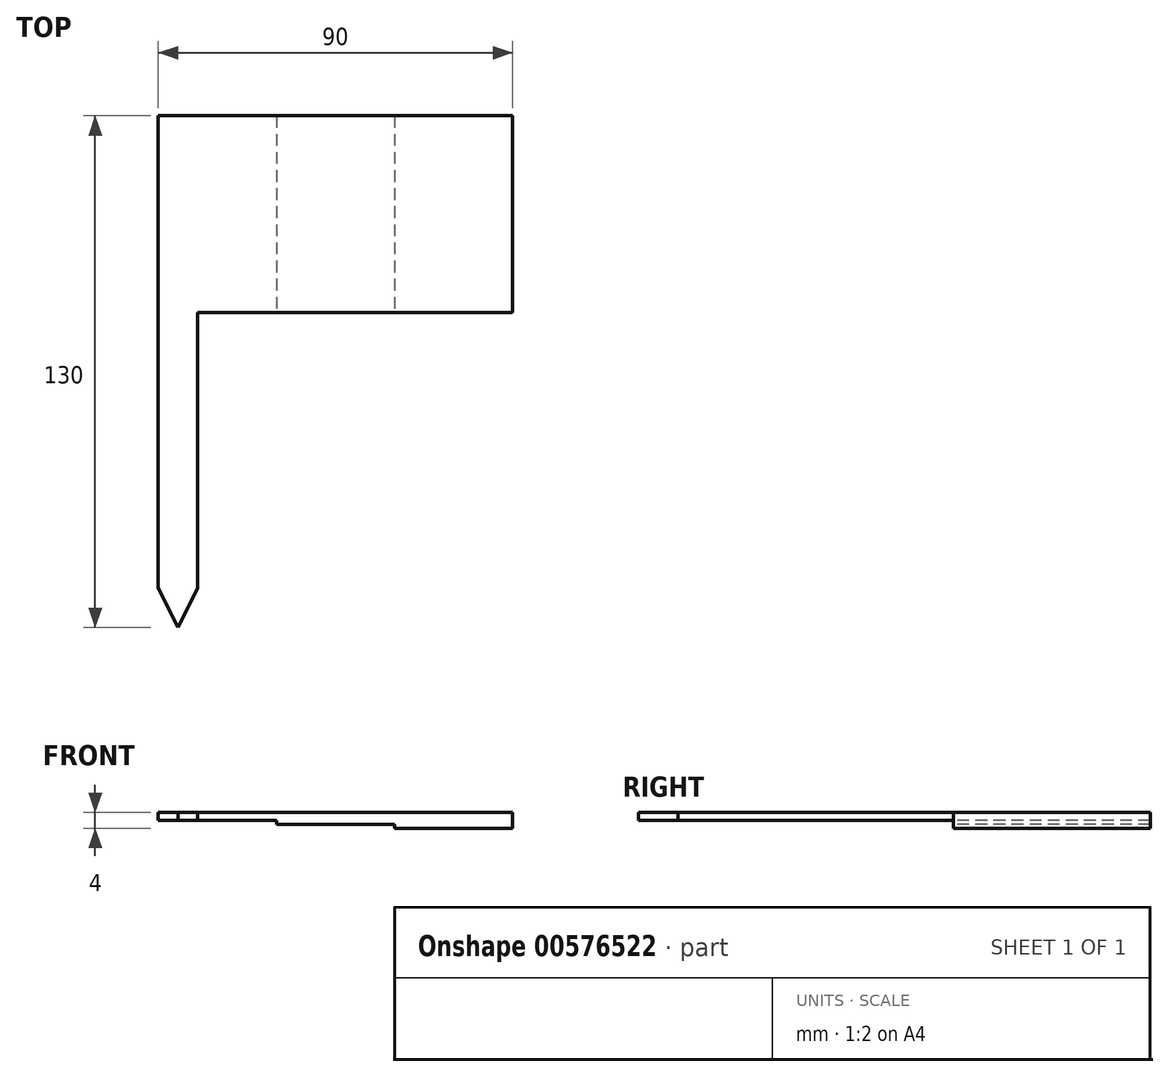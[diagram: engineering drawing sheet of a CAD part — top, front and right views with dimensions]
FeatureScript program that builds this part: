
annotation { "Feature Type Name" : "Feature", "Feature Type Description" : "" }
export const myFeature = defineFeature(function(context is Context, id is Id, definition is map)
    precondition{}
    {
        {
            var Q0;
            Q0=qCreatedBy(makeId("Top.planeOp"),FACE);
            var sketch = newSketch(context, id + "F0", { "sketchPlane" : qUnion([Q0])});
            skLineSegment(sketch, "E0.bottom", {"start": v(-47.33, 20.58) * mm, "end": v(42.67, 20.58) * mm});
            skLineSegment(sketch, "E0.top", {"start": v(-37.33, -29.42) * mm, "end": v(42.67, -29.42) * mm});
            skLineSegment(sketch, "E0.left", {"start": v(-47.33, 20.58) * mm, "end": v(-47.33, -29.42) * mm});
            skLineSegment(sketch, "E0.right", {"start": v(42.67, 20.58) * mm, "end": v(42.67, -29.42) * mm});
            skLineSegment(sketch, "E1.left", {"start": v(-47.33, -29.42) * mm, "end": v(-47.33, -99.42) * mm});
            skLineSegment(sketch, "E1.right", {"start": v(-37.33, -29.42) * mm, "end": v(-37.33, -99.42) * mm});
            skLineSegment(sketch, "E2", {"start": v(-47.33, -99.42) * mm, "end": v(-42.33, -109.42) * mm});
            skLineSegment(sketch, "E3", {"start": v(-37.33, -99.42) * mm, "end": v(-42.33, -109.42) * mm});
            skLineSegment(sketch, "E4.0", {"start": v(-17.33, 20.58) * mm, "end": v(-17.33, -29.42) * mm});
            skLineSegment(sketch, "E5.0", {"start": v(12.67, 20.58) * mm, "end": v(12.67, -29.42) * mm});
            skSolve(sketch);
        }
        {
            var Q0;
            {var subQ0=sQuery(id+"F0.wireOp",EDGE,"E0.left");Q0=makeQuery(id+"F0.imprint","IMPRINT",FACE,{"disambiguationData":[TD([[makeQuery(id+"F0.imprint","IMPRINT",EDGE,{"derivedFrom":subQ0}),1.0]])]});}
            extrude(context, id + "F1", {"entities" : qUnion([Q0]), "oppositeDirection" : true, "depth" : 2 * mm, "offsetDistance" : 25 * mm});
        }
        {
            var Q0;
            {var subQ0=sQuery(id+"F0.wireOp",EDGE,"E4.0");Q0=makeQuery(id+"F0.imprint","IMPRINT",FACE,{"disambiguationData":[TD([[makeQuery(id+"F0.imprint","IMPRINT",EDGE,{"derivedFrom":subQ0}),1.0]])]});}
            extrude(context, id + "F2", {"entities" : qUnion([Q0]), "operationType" : NewBodyOperationType.ADD, "oppositeDirection" : true, "depth" : 3 * mm, "offsetDistance" : 25 * mm});
        }
        {
            var Q0;
            {var subQ0=sQuery(id+"F0.wireOp",EDGE,"E0.right");Q0=makeQuery(id+"F0.imprint","IMPRINT",FACE,{"disambiguationData":[TD([[makeQuery(id+"F0.imprint","IMPRINT",EDGE,{"derivedFrom":subQ0}),-1.0]])]});}
            extrude(context, id + "F3", {"entities" : qUnion([Q0]), "operationType" : NewBodyOperationType.ADD, "oppositeDirection" : true, "depth" : 4 * mm, "offsetDistance" : 25 * mm});
        }
    });
